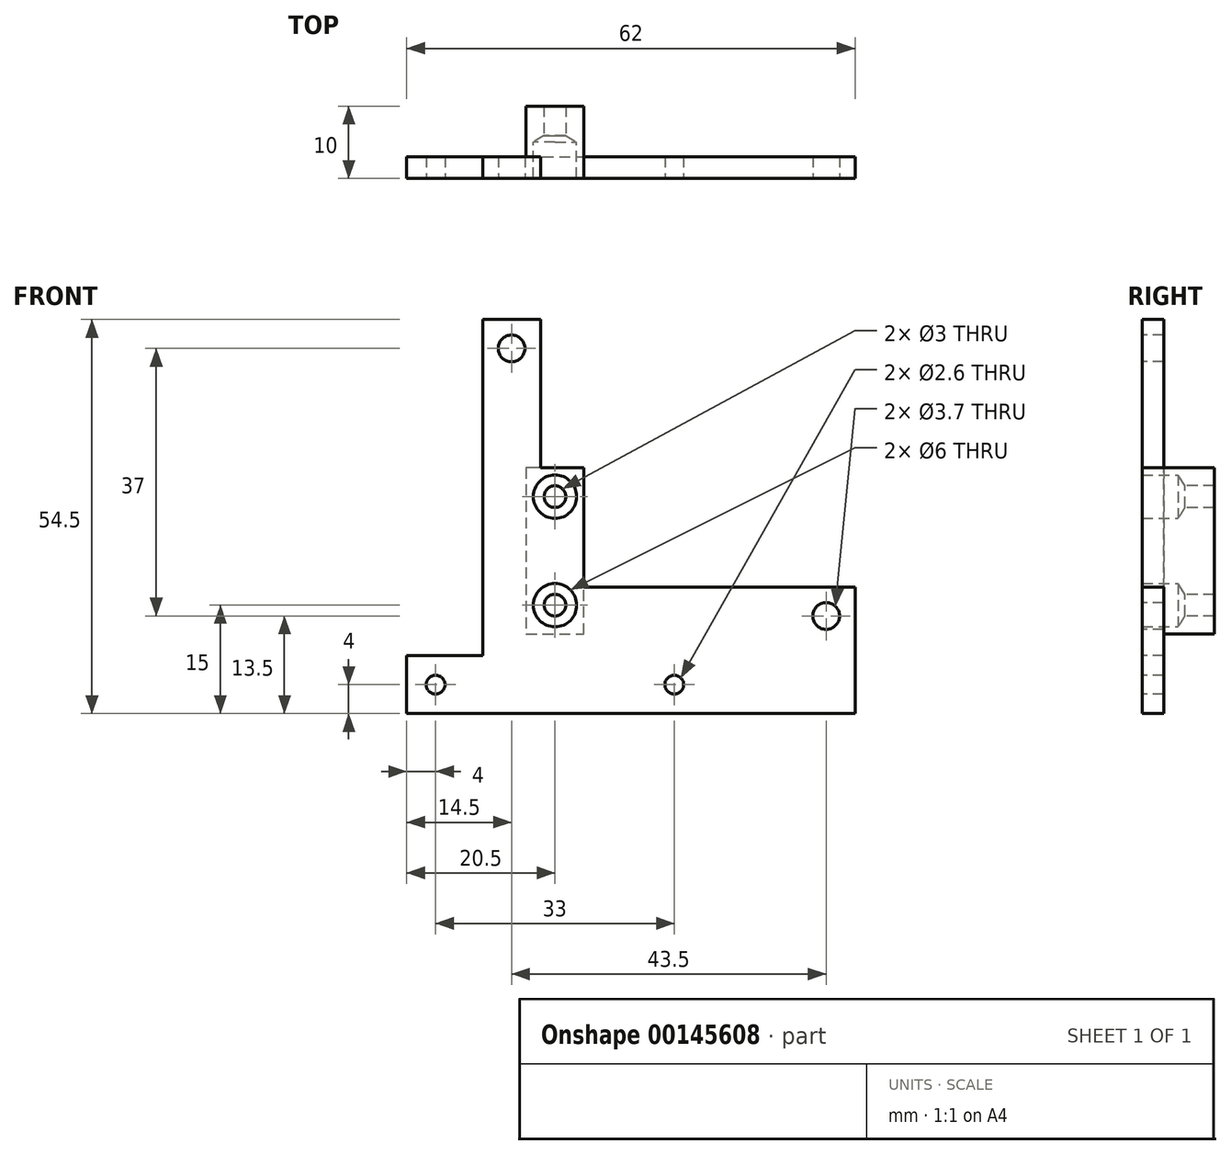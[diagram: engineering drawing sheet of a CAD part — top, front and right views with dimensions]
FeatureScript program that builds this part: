
annotation { "Feature Type Name" : "Feature", "Feature Type Description" : "" }
export const myFeature = defineFeature(function(context is Context, id is Id, definition is map)
    precondition{}
    {
        {
            var Q0;
            Q0=qCreatedBy(makeId("Front.planeOp"),FACE);
            var sketch = newSketch(context, id + "F0", { "sketchPlane" : qUnion([Q0])});
            skLineSegment(sketch, "E0", {"start": v(10, 73.44) * mm, "end": v(10, -53.24) * mm, "construction": true});
            skCircle(sketch, "E1", {"center": v(-6.5, -1) * mm, "radius": 1.3 * mm});
            skCircle(sketch, "E2", {"center": v(26.5, -1) * mm, "radius": 1.3 * mm});
            skCircle(sketch, "E3", {"center": v(4, 45.5) * mm, "radius": 1.85 * mm});
            skCircle(sketch, "E4", {"center": v(47.5, 8.5) * mm, "radius": 1.85 * mm});
            skLineSegment(sketch, "E5.right", {"start": v(10, 25) * mm, "end": v(10, 10) * mm, "construction": true});
            skCircle(sketch, "E6", {"center": v(10, 25) * mm, "radius": 1.5 * mm});
            skCircle(sketch, "E7", {"center": v(10, 10) * mm, "radius": 1.5 * mm});
            skLineSegment(sketch, "E8", {"start": v(51.5, -5) * mm, "end": v(51.5, 12.5) * mm});
            skLineSegment(sketch, "E9", {"start": v(51.5, 12.5) * mm, "end": v(14, 12.5) * mm});
            skLineSegment(sketch, "E10", {"start": v(14, 12.5) * mm, "end": v(14, 29) * mm});
            skLineSegment(sketch, "E11", {"start": v(14, 29) * mm, "end": v(8, 29) * mm});
            skLineSegment(sketch, "E12", {"start": v(8, 29) * mm, "end": v(8, 49.5) * mm});
            skLineSegment(sketch, "E13", {"start": v(8, 49.5) * mm, "end": v(0, 49.5) * mm});
            skLineSegment(sketch, "E14", {"start": v(0, 3) * mm, "end": v(-10.5, 3) * mm});
            skLineSegment(sketch, "E15", {"start": v(51.5, -5) * mm, "end": v(-10.5, -5) * mm});
            skPoint(sketch, "E16", {"position": v(0, 3) * mm});
            skLineSegment(sketch, "E17", {"start": v(0, 3) * mm, "end": v(0, 49.5) * mm});
            skLineSegment(sketch, "E18", {"start": v(-10.5, -5) * mm, "end": v(-10.5, 3) * mm});
            skLineSegment(sketch, "E19", {"start": v(6, 29) * mm, "end": v(6, 6) * mm});
            skLineSegment(sketch, "E20", {"start": v(6, 6) * mm, "end": v(14, 6) * mm});
            skLineSegment(sketch, "E21", {"start": v(14, 6) * mm, "end": v(14, 12.5) * mm});
            skLineSegment(sketch, "E22", {"start": v(8, 29) * mm, "end": v(6, 29) * mm});
            skSolve(sketch);
        }
        {
            var Q0;
            Q0=qSketchRegion(id+"F0",true);
            extrude(context, id + "F1", {"entities" : qUnion([Q0]), "oppositeDirection" : true, "depth" : 3 * mm, "offsetDistance" : 25 * mm});
        }
        {
            var Q0;
            Q0=makeQuery(id+"F0.imprint","IMPRINT",FACE,{"disambiguationData":[TD([[makeQuery(id+"F0.imprint","IMPRINT",EDGE,{"derivedFrom":sQuery(id+"F0.wireOp",EDGE,"E6")}),-1.0]])]});
            extrude(context, id + "F2", {"entities" : qUnion([Q0]), "operationType" : NewBodyOperationType.ADD, "oppositeDirection" : true, "depth" : 10 * mm, "offsetDistance" : 25 * mm});
        }
        {
            var Q0;
            Q0=sQuery(id+"F0.wireOp",VERTEX,"E6.center");
            var Q1;
            Q1=sQuery(id+"F0.wireOp",VERTEX,"E7.center");
            var Q2;
            Q2=makeQuery(id+"F1.opExtrude","SWEPT_BODY",BODY,{"disambiguationData":[OSD([sQuery(id+"F0.wireOp",EDGE,"E1"),sQuery(id+"F0.wireOp",EDGE,"E2"),sQuery(id+"F0.wireOp",EDGE,"E3"),sQuery(id+"F0.wireOp",EDGE,"E4"),sQuery(id+"F0.wireOp",EDGE,"E6"),sQuery(id+"F0.wireOp",EDGE,"E7"),sQuery(id+"F0.wireOp",EDGE,"E8"),sQuery(id+"F0.wireOp",EDGE,"E9"),sQuery(id+"F0.wireOp",EDGE,"E10"),sQuery(id+"F0.wireOp",EDGE,"E11"),sQuery(id+"F0.wireOp",EDGE,"E12"),sQuery(id+"F0.wireOp",EDGE,"E13"),sQuery(id+"F0.wireOp",EDGE,"E14"),sQuery(id+"F0.wireOp",EDGE,"E15"),sQuery(id+"F0.wireOp",EDGE,"E17"),sQuery(id+"F0.wireOp",EDGE,"E18")])]});
            hole(context, id + "F3", {"style" : HoleStyle.SIMPLE, "endStyle" : HoleEndStyle.BLIND, "holeDiameter" : 6 * mm, "holeDepth" : 5 * mm, "tappedDepth" : 12 * mm, "tapClearance" : 3, "locations" : qUnion([Q0, Q1]), "scope" : qUnion([Q2]), "majorDiameter" : 5 * mm});
        }
    });
